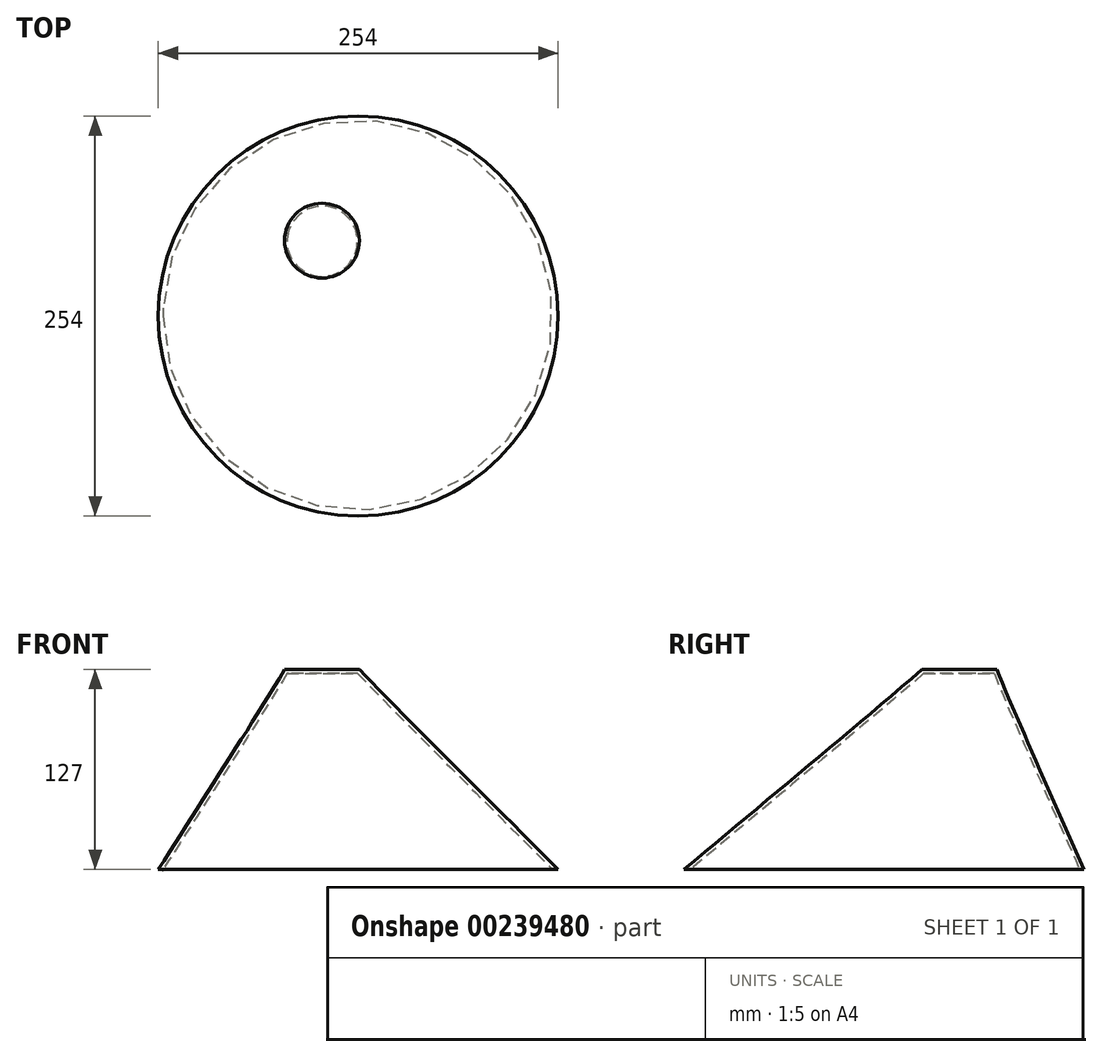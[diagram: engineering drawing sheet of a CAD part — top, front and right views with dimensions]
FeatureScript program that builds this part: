
annotation { "Feature Type Name" : "Feature", "Feature Type Description" : "" }
export const myFeature = defineFeature(function(context is Context, id is Id, definition is map)
    precondition{}
    {
        {
            var Q0;
            Q0=qCreatedBy(makeId("Top.planeOp"),FACE);
            cPlane(context, id + "F0", {"entities" : qUnion([Q0]), "cplaneType" : CPlaneType.OFFSET, "offset" : 127 * mm, "width" : 152.4 * mm, "height" : 152.4 * mm});
        }
        {
            var Q0;
            Q0=qCreatedBy(makeId("Top.planeOp"),FACE);
            var sketch = newSketch(context, id + "F1", { "sketchPlane" : qUnion([Q0])});
            skCircle(sketch, "E0", {"center": v(0, 0) * mm, "radius": 127 * mm});
            skSolve(sketch);
        }
        {
            var Q0;
            Q0=qCreatedBy(id+"F0.planeOp",FACE);
            var sketch = newSketch(context, id + "F2", { "sketchPlane" : qUnion([Q0])});
            skCircle(sketch, "E1", {"center": v(-23.03, 47.9) * mm, "radius": 23.74 * mm});
            skSolve(sketch);
        }
        {
            var Q0;
            Q0=makeQuery(id+"F1.imprint","IMPRINT",FACE,{"disambiguationData":[TD([[makeQuery(id+"F1.imprint","IMPRINT",EDGE,{"derivedFrom":sQuery(id+"F1.wireOp",EDGE,"E0")}),1.0]])]});
            var Q1;
            Q1=makeQuery(id+"F2.imprint","IMPRINT",FACE,{"disambiguationData":[TD([[makeQuery(id+"F2.imprint","IMPRINT",EDGE,{"derivedFrom":sQuery(id+"F2.wireOp",EDGE,"E1")}),1.0]])]});
            loft(context, id + "F3", {"sheetProfilesArray" : [{ "sheetProfileEntities" : qUnion([Q0]) }, { "sheetProfileEntities" : qUnion([Q1]) }]});
        }
        {
            var Q0;
            Q0=makeQuery(id+"F3.opLoft","CAP_FACE",FACE,{"disambiguationData":[OSD([makeQuery(id+"F1.imprint","IMPRINT",FACE,{"disambiguationData":[TD([[makeQuery(id+"F1.imprint","IMPRINT",EDGE,{"derivedFrom":sQuery(id+"F1.wireOp",EDGE,"E0")}),1.0]])]})])],"isStart":true});
            shell(context, id + "F4", {"entities" : qUnion([Q0]), "thickness" : 2.54 * mm});
        }
    });
